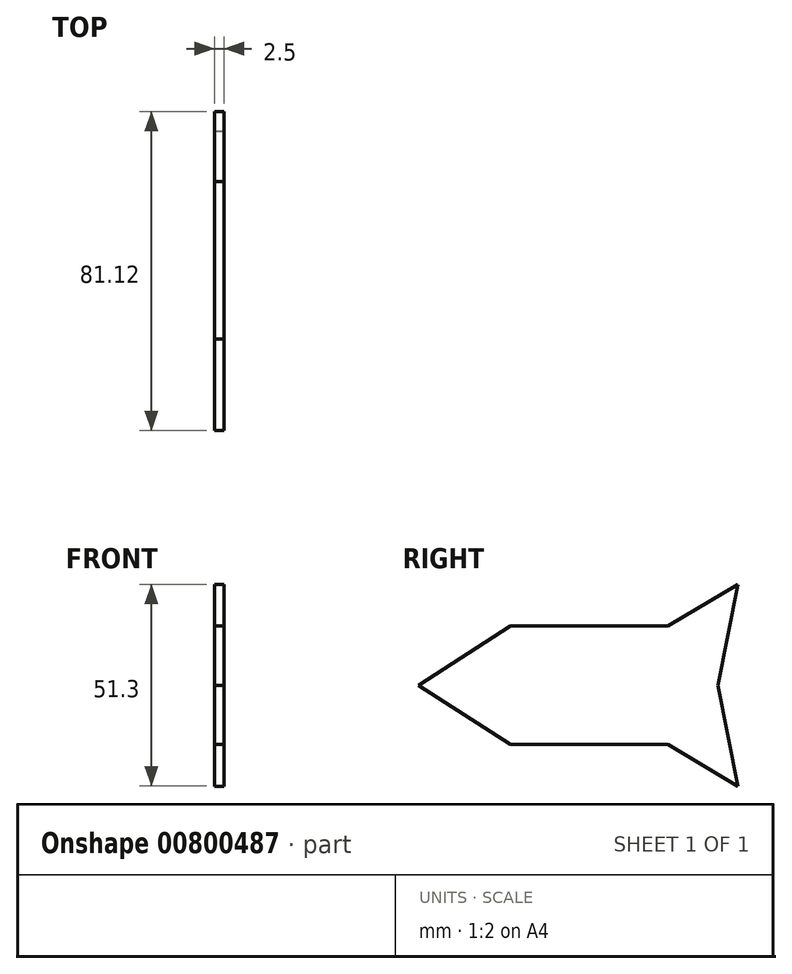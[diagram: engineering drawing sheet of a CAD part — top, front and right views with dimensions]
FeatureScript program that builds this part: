
annotation { "Feature Type Name" : "Feature", "Feature Type Description" : "" }
export const myFeature = defineFeature(function(context is Context, id is Id, definition is map)
    precondition{}
    {
        {
            var Q0;
            Q0=qCreatedBy(makeId("Right.planeOp"),FACE);
            var sketch = newSketch(context, id + "F0", { "sketchPlane" : qUnion([Q0])});
            skLineSegment(sketch, "E0.bottom", {"start": v(-20, 15) * mm, "end": v(20, 15) * mm});
            skLineSegment(sketch, "E0.top", {"start": v(-20, -15) * mm, "end": v(20, -15) * mm});
            skPoint(sketch, "E0.middle", {"position": v(0, 0) * mm});
            skLineSegment(sketch, "E1", {"start": v(-20, 15) * mm, "end": v(-43.3, 0) * mm});
            skLineSegment(sketch, "E2", {"start": v(20, 15) * mm, "end": v(37.83, 25.65) * mm});
            skLineSegment(sketch, "E3", {"start": v(37.83, 25.65) * mm, "end": v(32.73, 0) * mm});
            skPoint(sketch, "E3.endSnap0", {"position": v(20, 0) * mm});
            skLineSegment(sketch, "E4.MirrorCS", {"start": v(-20, -15) * mm, "end": v(-43.3, 0) * mm});
            skLineSegment(sketch, "E5.MirrorCS", {"start": v(20, -15) * mm, "end": v(37.83, -25.65) * mm});
            skLineSegment(sketch, "E6.MirrorCS", {"start": v(37.83, -25.65) * mm, "end": v(32.73, 0) * mm});
            skSolve(sketch);
        }
        {
            var Q0;
            Q0=makeQuery(id+"F0.imprint","IMPRINT",FACE,{"disambiguationData":[TD([[makeQuery(id+"F0.imprint","IMPRINT",EDGE,{"derivedFrom":sQuery(id+"F0.wireOp",EDGE,"E0.bottom")}),-1.0]])]});
            extrude(context, id + "F1", {"entities" : qUnion([Q0]), "depth" : 2.5 * mm, "offsetDistance" : 25 * mm});
        }
    });
